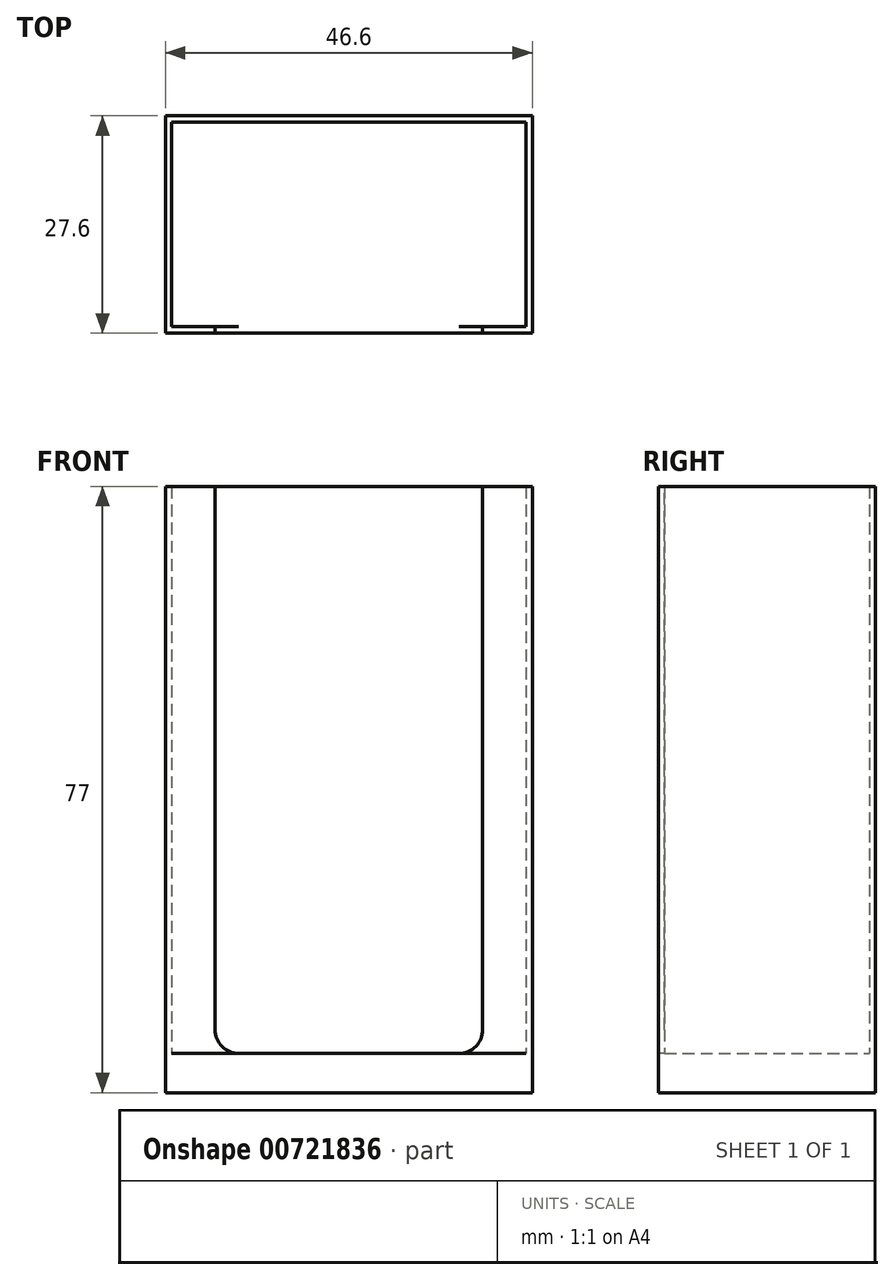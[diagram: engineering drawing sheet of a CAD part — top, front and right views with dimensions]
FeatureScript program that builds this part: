
annotation { "Feature Type Name" : "Feature", "Feature Type Description" : "" }
export const myFeature = defineFeature(function(context is Context, id is Id, definition is map)
    precondition{}
    {
        {
            var Q0;
            Q0=qCreatedBy(makeId("Top.planeOp"),FACE);
            var sketch = newSketch(context, id + "F0", { "sketchPlane" : qUnion([Q0])});
            skLineSegment(sketch, "E0.bottom", {"start": v(22.5, 13) * mm, "end": v(-22.5, 13) * mm});
            skLineSegment(sketch, "E0.top", {"start": v(22.5, -13) * mm, "end": v(-22.5, -13) * mm});
            skLineSegment(sketch, "E0.left", {"start": v(22.5, 13) * mm, "end": v(22.5, -13) * mm});
            skLineSegment(sketch, "E0.right", {"start": v(-22.5, 13) * mm, "end": v(-22.5, -13) * mm});
            skPoint(sketch, "E0.middle", {"position": v(0, 0) * mm});
            skLineSegment(sketch, "E1.bottom", {"start": v(23.3, 13.8) * mm, "end": v(-23.3, 13.8) * mm});
            skLineSegment(sketch, "E1.top", {"start": v(23.3, -13.8) * mm, "end": v(-23.3, -13.8) * mm});
            skLineSegment(sketch, "E1.left", {"start": v(23.3, 13.8) * mm, "end": v(23.3, -13.8) * mm});
            skLineSegment(sketch, "E1.right", {"start": v(-23.3, 13.8) * mm, "end": v(-23.3, -13.8) * mm});
            skSolve(sketch);
        }
        {
            var Q0;
            Q0 = qSketchRegion(id + "F0", true);
            extrude(context, id + "F1", {"entities" : qUnion([Q0]), "depth" : 77 * mm, "offsetDistance" : 25 * mm});
        }
        {
            var Q0;
            Q0=makeQuery(id+"F1.opExtrude","CAP_FACE",FACE,{"disambiguationData":[OSD([sQuery(id+"F0.wireOp",EDGE,"E0.bottom"),sQuery(id+"F0.wireOp",EDGE,"E0.top"),sQuery(id+"F0.wireOp",EDGE,"E0.left"),sQuery(id+"F0.wireOp",EDGE,"E0.right"),sQuery(id+"F0.wireOp",EDGE,"E1.bottom"),sQuery(id+"F0.wireOp",EDGE,"E1.top"),sQuery(id+"F0.wireOp",EDGE,"E1.left"),sQuery(id+"F0.wireOp",EDGE,"E1.right")])],"isStart":true});
            var sketch = newSketch(context, id + "F2", { "sketchPlane" : qUnion([Q0])});
            skLineSegment(sketch, "E2.0", {"start": v(-23.3, -13.8) * mm, "end": v(-23.3, 13.8) * mm});
            skLineSegment(sketch, "E2.1", {"start": v(23.3, 13.8) * mm, "end": v(-23.3, 13.8) * mm});
            skLineSegment(sketch, "E2.2", {"start": v(23.3, -13.8) * mm, "end": v(-23.3, -13.8) * mm});
            skLineSegment(sketch, "E2.3", {"start": v(23.3, -13.8) * mm, "end": v(23.3, 13.8) * mm});
            skSolve(sketch);
        }
        {
            var Q0;
            Q0 = qSketchRegion(id + "F2", true);
            extrude(context, id + "F3", {"entities" : qUnion([Q0]), "operationType" : NewBodyOperationType.ADD, "oppositeDirection" : true, "depth" : 5 * mm, "offsetDistance" : 25 * mm});
        }
        {
            var Q0;
            Q0=makeQuery(id+"F1.opExtrude","SWEPT_FACE",FACE,{"disambiguationData":[OSD([sQuery(id+"F0.wireOp",EDGE,"E1.top")])]});
            var sketch = newSketch(context, id + "F4", { "sketchPlane" : qUnion([Q0])});
            skLineSegment(sketch, "E3.bottom", {"start": v(17, 77) * mm, "end": v(-17, 77) * mm});
            skLineSegment(sketch, "E3.top", {"start": v(17, 5) * mm, "end": v(-17, 5) * mm});
            skLineSegment(sketch, "E3.left", {"start": v(17, 77) * mm, "end": v(17, 5) * mm});
            skLineSegment(sketch, "E3.right", {"start": v(-17, 77) * mm, "end": v(-17, 5) * mm});
            skPoint(sketch, "E3.middle", {"position": v(0, 41) * mm});
            skSolve(sketch);
        }
        {
            var Q0;
            Q0 = qSketchRegion(id + "F4", true);
            extrude(context, id + "F5", {"entities" : qUnion([Q0]), "operationType" : NewBodyOperationType.REMOVE, "endBound" : BoundingType.UP_TO_NEXT, "oppositeDirection" : true, "depth" : 25 * mm, "offsetDistance" : 25 * mm});
        }
        {
            var Q0;
            Q0=makeQuery(id+"F5.boolean.opBoolean","COPY",EDGE,{"derivedFrom":makeQuery(id+"F5.opExtrude","SWEPT_EDGE",EDGE,{"disambiguationData":[OSD([sQuery(id+"F0.wireOp",EDGE,"E1.top"),sQuery(id+"F4.wireOp",EDGE,"E3.bottom"),sQuery(id+"F4.wireOp",EDGE,"E3.right")])]})});
            var Q1;
            Q1=makeQuery(id+"F5.boolean.opBoolean","COPY",EDGE,{"derivedFrom":makeQuery(id+"F5.opExtrude","SWEPT_EDGE",EDGE,{"disambiguationData":[OSD([sQuery(id+"F0.wireOp",EDGE,"E1.top"),sQuery(id+"F4.wireOp",EDGE,"E3.bottom"),sQuery(id+"F4.wireOp",EDGE,"E3.left")])]})});
            var Q2;
            Q2=makeQuery(id+"F5.boolean.opBoolean","COPY",EDGE,{"derivedFrom":makeQuery(id+"F5.opExtrude","SWEPT_EDGE",EDGE,{"disambiguationData":[OSD([sQuery(id+"F4.wireOp",EDGE,"E3.top"),sQuery(id+"F4.wireOp",EDGE,"E3.right")])]})});
            var Q3;
            Q3=makeQuery(id+"F5.boolean.opBoolean","COPY",EDGE,{"derivedFrom":makeQuery(id+"F5.opExtrude","SWEPT_EDGE",EDGE,{"disambiguationData":[OSD([sQuery(id+"F4.wireOp",EDGE,"E3.top"),sQuery(id+"F4.wireOp",EDGE,"E3.left")])]})});
            fillet(context, id + "F6", {"entities" : qUnion([Q0, Q1, Q2, Q3]), "radius" : 3 * mm, "tangentPropagation" : true, "allowEdgeOverflow" : false});
        }
    });
